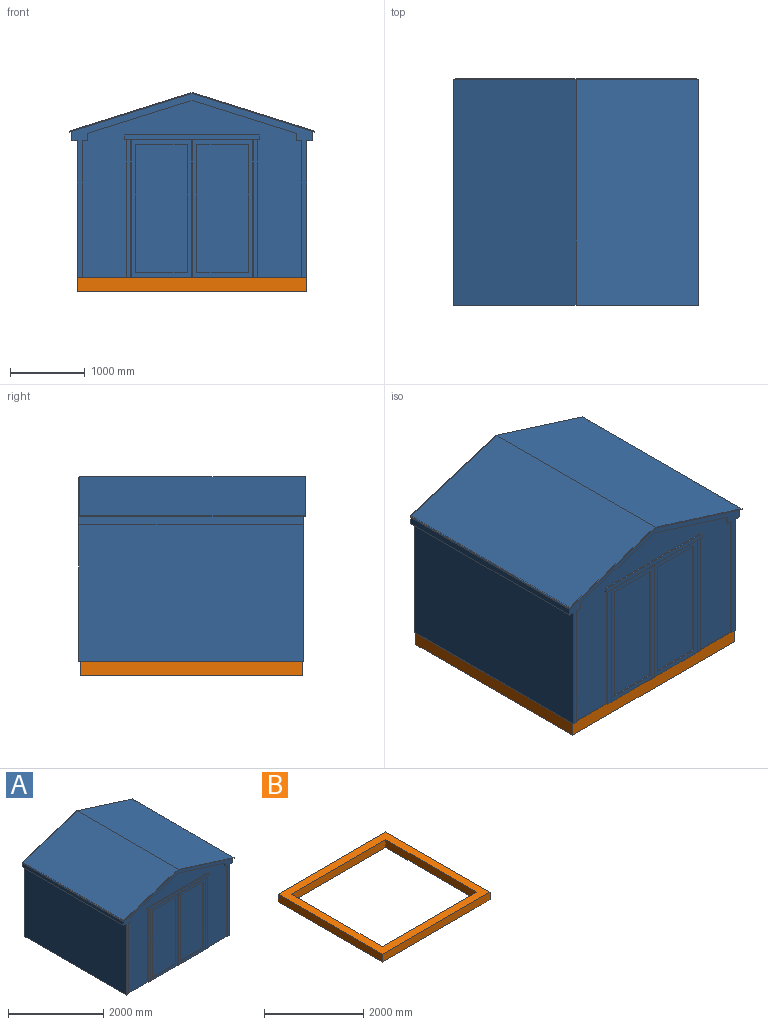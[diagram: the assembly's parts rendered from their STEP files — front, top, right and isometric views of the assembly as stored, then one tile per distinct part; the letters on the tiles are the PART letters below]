
ASSEMBLY  parts=2 mates=1
PART A: 83 faces, bbox 3276.6x3035.3x2477.1 mm
  f0: plane 2946.4x2108.2mm, normal (0,1,0), area 5815966.2mm2, adj f6,f30,f33,f34,f35,f36,f38,f39
  f1: plane 2946.4x2370.59mm, normal (0,-1,0), area 2944735.7mm2, adj f6,f8,f9,f10,f11,f13,f14,f19
  f2: plane 1612.9x508mm, normal (-0.3,0,0.95), area 21475.8mm2, adj f3,f37,f47,f48
  f3: plane 3009.9x127mm, normal (-1,0,0), area 382257.3mm2, adj f2,f4,f12,f37,f43
  f4: plane 3009.9x76.2mm, normal (0,0,-1), area 229354.4mm2, adj f3,f5,f12,f37
  f5: plane 3009.9x1828.8mm, normal (-1,0,0), area 5504505.1mm2, adj f4,f6,f12,f37
  f6: plane 3073.4x3009.9mm, normal (0,0,-1), area 9171755.8mm2, adj f0,f1,f5,f8,f12,f13,f19,f20
  f7: plane 1262.98x198.89mm, normal (0,1,0), area 125600.3mm2, adj f31,f32,f71
  f8: plane 1828.8x19.05mm, normal (1,0,0), area 34838.6mm2, adj f1,f6,f9,f12
  f9: plane 76.2x19.05mm, normal (0,0,-1), area 1451.6mm2, adj f1,f8,f10,f12
  f10: plane 101.79x19.05mm, normal (1,0,0), area 1939.2mm2, adj f1,f9,f11,f12
  f11: plane 1397x440mm, normal (0.3,0,-0.95), area 27901.6mm2, adj f1,f10,f12,f55
  f12: plane 3225.8x2463.8mm, normal (0,-1,0), area 562192.7mm2, adj f3,f4,f5,f6,f8,f9,f10,f11
  f13: plane 1841.5x19.05mm, normal (1,0,0), area 35080.6mm2, adj f1,f6,f14,f20
  f14: plane 812.8x19.05mm, normal (0,0,1), area 15483.8mm2, adj f1,f13,f19,f20
  f15: plane 685.8x19.05mm, normal (0,0,-1), area 13064.5mm2, adj f16,f18,f20,f21
  f16: plane 1714.5x19.05mm, normal (-1,0,0), area 32661.2mm2, adj f15,f17,f20,f21
  f17: plane 685.8x19.05mm, normal (0,0,1), area 13064.5mm2, adj f16,f18,f20,f21
  f18: plane 1714.5x19.05mm, normal (1,0,0), area 32661.2mm2, adj f15,f17,f20,f21
  f19: plane 1841.5x19.05mm, normal (-1,0,0), area 35080.6mm2, adj f1,f6,f14,f20
  f20: plane 1841.5x812.8mm, normal (0,-1,0), area 320967.1mm2, adj f6,f13,f14,f15,f16,f17,f18,f19
  f21: plane 1714.5x685.8mm, normal (0,-1,0), area 1175804.1mm2, adj f15,f16,f17,f18
  f22: plane 63.5x19.05mm, normal (0,0,1), area 1209.7mm2, adj f1,f23,f24,f25
  f23: plane 1841.5x19.05mm, normal (-1,0,0), area 35080.6mm2, adj f1,f6,f22,f25
  f24: plane 1841.5x19.05mm, normal (1,0,0), area 35080.6mm2, adj f1,f6,f22,f25
  f25: plane 1841.5x63.5mm, normal (0,-1,0), area 116935.2mm2, adj f6,f22,f23,f24
  f26: plane 1816.1x19.05mm, normal (0,0,1), area 34596.7mm2, adj f1,f27,f29,f69
  f27: plane 63.5x19.05mm, normal (-1,0,0), area 1209.7mm2, adj f1,f26,f28,f29
  f28: plane 1816.1x19.05mm, normal (0,0,-1), area 34596.7mm2, adj f1,f27,f29,f69
  f29: plane 1816.1x63.5mm, normal (0,-1,0), area 115322.4mm2, adj f26,f27,f28,f69
  f30: plane 1828.8x19.05mm, normal (1,0,0), area 34838.6mm2, adj f0,f6,f36,f37
  f31: plane 631.49x198.89mm, normal (0.3,0,-0.95), area 12612.5mm2, adj f7,f32,f37,f71
  f32: plane 1262.98x19.05mm, normal (0,0,1), area 24059.8mm2, adj f7,f31,f37,f71
  f33: plane 1666.21x19.05mm, normal (0,0,-1), area 31741.2mm2, adj f0,f34,f37,f72
  f34: plane 563.9x177.61mm, normal (0.3,0,-0.95), area 11262.4mm2, adj f0,f33,f35,f37
  f35: plane 101.79x19.05mm, normal (1,0,0), area 1939.2mm2, adj f0,f34,f36,f37
  f36: plane 76.2x19.05mm, normal (0,0,-1), area 1451.6mm2, adj f0,f30,f35,f37
  f37: plane 3225.8x2463.8mm, normal (0,1,0), area 655194.5mm2, adj f2,f3,f4,f5,f6,f30,f31,f32
  f38: plane 355.6x6.35mm, normal (0,0,1), area 2258.1mm2, adj f0,f39,f41,f42
  f39: plane 355.6x6.35mm, normal (1,0,0), area 2258.1mm2, adj f0,f38,f40,f42
  f40: plane 355.6x6.35mm, normal (0,0,-1), area 2258.1mm2, adj f0,f39,f41,f42
  f41: plane 355.6x6.35mm, normal (-1,0,0), area 2258.1mm2, adj f0,f38,f40,f42
  f42: plane 355.6x355.6mm, normal (0,1,0), area 126451.4mm2, adj f38,f39,f40,f41
  f43: plane 3022.6x1638.3mm, normal (0.3,0,-0.95), area 123443.6mm2, adj f3,f12,f45,f46,f47,f80
  f44: plane 3022.6x1638.3mm, normal (-0.3,0,0.95), area 5191734.9mm2, adj f45,f46,f47,f81
  f45: plane 3022.6x13.32mm, normal (-1,0,0), area 40246mm2, adj f43,f44,f46,f47
  f46: plane 3276.6x529.32mm, normal (0,-1,0), area 43628mm2, adj f43,f44,f45,f80,f81,f82
  f47: plane 3276.6x529.32mm, normal (0,1,0), area 43628mm2, adj f2,f43,f44,f45,f48,f80,f81,f82
  f48: plane 1612.9x508mm, normal (0.3,0,0.95), area 21475.8mm2, adj f2,f37,f47,f49
  f49: plane 3009.9x127mm, normal (1,0,0), area 382257.3mm2, adj f12,f37,f48,f50,f80
  f50: plane 3009.9x76.2mm, normal (0,0,-1), area 229354.4mm2, adj f12,f37,f49,f51
  f51: plane 3009.9x1828.8mm, normal (1,0,0), area 5504505.1mm2, adj f6,f12,f37,f50
  f52: plane 1828.8x19.05mm, normal (-1,0,0), area 34838.6mm2, adj f1,f6,f12,f53
  f53: plane 76.2x19.05mm, normal (0,0,-1), area 1451.6mm2, adj f1,f12,f52,f54
  f54: plane 101.79x19.05mm, normal (-1,0,0), area 1939.2mm2, adj f1,f12,f53,f55
  f55: plane 1397x440mm, normal (-0.3,0,-0.95), area 27901.6mm2, adj f1,f11,f12,f54
  f56: plane 1841.5x19.05mm, normal (-1,0,0), area 35080.6mm2, adj f1,f6,f57,f63
  f57: plane 812.8x19.05mm, normal (0,0,1), area 15483.8mm2, adj f1,f56,f62,f63
  f58: plane 685.8x19.05mm, normal (0,0,-1), area 13064.5mm2, adj f59,f61,f63,f64
  f59: plane 1714.5x19.05mm, normal (1,0,0), area 32661.2mm2, adj f58,f60,f63,f64
  f60: plane 685.8x19.05mm, normal (0,0,1), area 13064.5mm2, adj f59,f61,f63,f64
  f61: plane 1714.5x19.05mm, normal (-1,0,0), area 32661.2mm2, adj f58,f60,f63,f64
  f62: plane 1841.5x19.05mm, normal (1,0,0), area 35080.6mm2, adj f1,f6,f57,f63
  f63: plane 1841.5x812.8mm, normal (0,-1,0), area 320967.1mm2, adj f6,f56,f57,f58,f59,f60,f61,f62
  f64: plane 1714.5x685.8mm, normal (0,-1,0), area 1175804.1mm2, adj f58,f59,f60,f61
  f65: plane 63.5x19.05mm, normal (0,0,1), area 1209.7mm2, adj f1,f66,f67,f68
  f66: plane 1841.5x19.05mm, normal (1,0,0), area 35080.6mm2, adj f1,f6,f65,f68
  f67: plane 1841.5x19.05mm, normal (-1,0,0), area 35080.6mm2, adj f1,f6,f65,f68
  f68: plane 1841.5x63.5mm, normal (0,-1,0), area 116935.2mm2, adj f6,f65,f66,f67
  f69: plane 63.5x19.05mm, normal (1,0,0), area 1209.7mm2, adj f1,f26,f28,f29
  f70: plane 1828.8x19.05mm, normal (-1,0,0), area 34838.6mm2, adj f0,f6,f37,f74
  f71: plane 631.49x198.89mm, normal (-0.3,0,-0.95), area 12612.5mm2, adj f7,f31,f32,f37
  f72: plane 563.9x177.61mm, normal (-0.3,0,-0.95), area 11262.4mm2, adj f0,f33,f37,f73
  f73: plane 101.79x19.05mm, normal (-1,0,0), area 1939.2mm2, adj f0,f37,f72,f74
  f74: plane 76.2x19.05mm, normal (0,0,-1), area 1451.6mm2, adj f0,f37,f70,f73
  f75: plane 355.6x6.35mm, normal (0,0,1), area 2258.1mm2, adj f0,f76,f78,f79
  f76: plane 355.6x6.35mm, normal (-1,0,0), area 2258.1mm2, adj f0,f75,f77,f79
  f77: plane 355.6x6.35mm, normal (0,0,-1), area 2258.1mm2, adj f0,f76,f78,f79
  f78: plane 355.6x6.35mm, normal (1,0,0), area 2258.1mm2, adj f0,f75,f77,f79
  f79: plane 355.6x355.6mm, normal (0,1,0), area 126451.4mm2, adj f75,f76,f77,f78
  f80: plane 3022.6x1638.3mm, normal (-0.3,0,-0.95), area 123443.6mm2, adj f12,f43,f46,f47,f49,f82
  f81: plane 3022.6x1638.3mm, normal (0.3,0,0.95), area 5191734.9mm2, adj f44,f46,f47,f82
  f82: plane 3022.6x13.32mm, normal (1,0,0), area 40246mm2, adj f46,f47,f80,f81
PART B: 10 faces, bbox 3073.4x2971.8x190.5 mm
  f0: plane 3073.4x190.5mm, normal (0,1,0), area 585482.7mm2, adj f1,f4,f5,f6
  f1: plane 2971.8x190.5mm, normal (-1,0,0), area 566127.9mm2, adj f0,f4,f5,f8
  f2: plane 2590.8x190.5mm, normal (1,0,0), area 493547.4mm2, adj f3,f4,f5,f9
  f3: plane 2692.4x190.5mm, normal (0,-1,0), area 512902.2mm2, adj f2,f4,f5,f7
  f4: plane 3073.4x2971.8mm, normal (0,0,1), area 2158060.2mm2, adj f0,f1,f2,f3,f6,f7,f8,f9
  f5: plane 3073.4x2971.8mm, normal (0,0,-1), area 2158060.2mm2, adj f0,f1,f2,f3,f6,f7,f8,f9
  f6: plane 2971.8x190.5mm, normal (1,0,0), area 566127.9mm2, adj f0,f4,f5,f8
  f7: plane 2590.8x190.5mm, normal (-1,0,0), area 493547.4mm2, adj f3,f4,f5,f9
  f8: plane 3073.4x190.5mm, normal (0,-1,0), area 585482.7mm2, adj f1,f4,f5,f6
  f9: plane 2692.4x190.5mm, normal (0,1,0), area 512902.2mm2, adj f2,f4,f5,f7
PLACE A t=(94.95,2977.24,1135.18)mm
PLACE B t=(7498.59,484.02,0)mm
MATE fastened A.f6 <-> B.f4  axis (0,0,-1) through (1536.7,1485.9,190.5)mm
